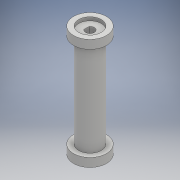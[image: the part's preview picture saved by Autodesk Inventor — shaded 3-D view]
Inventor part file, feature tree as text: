
AUTODESK INVENTOR PART (.ipt)
format: ipt  version: 2017 (Build 210142000, 142)  size: 198,144 bytes
history: native  units: mm
features: sketch x7, extrude x6, revolve x1
ambient origin geometry x8: Origin, YZ Plane, XZ Plane, XY Plane, X Axis, Y Axis, Z Axis, Center Point
bodies: Body1 (feature_tree)
feature tree (14):
  revolve  "Revolution2"  [1 undecoded]
  extrude  "Extrusion6"  Depth=20.0mm
  extrude  "Extrusion7"  Depth=4.0mm
  extrude  "Extrusion11"  Depth=2.5mm
  extrude  "Extrusion12"  Depth=4.0mm
  extrude  "Extrusion13"  Depth=20.0mm
  extrude  "Extrusion14"  Depth=15.0mm
  sketch  "Sketch1"  dims[d1=2.5mm d2=4.0mm]
  sketch  "Sketch6"  dims[d3=7.0mm d4=20.0mm]
  sketch  "Sketch7"  dims[d5=34.0mm d9=4.0mm]
  sketch  "Sketch11"  dims[d12=2.5mm d13=4.0mm]
  sketch  "Sketch12"  dims[d55=22.5mm d56=4.0mm]
  sketch  "Sketch13"  dims[d57=90.0deg d64=20.0mm]
  sketch  "Sketch14"  dims[d65=90.0deg d69=15.0mm d71=15.0mm d73=5.0mm d74=0.0mm d75=2.5mm d76=5.0mm d77=5.0mm d78=26.0mm d79=0.0mm d80=3.0mm d81=3.0mm d82=3.0mm d83=3.0mm d90=19.0mm d91=100.0mm d92=0.0mm d93=2.0mm d94=0.0mm d95=30.0mm d96=0.0mm d97=19.0mm d98=13.0mm d99=2.0mm d100=0.0mm]
note: 1 required parameter value undecoded (feature->parameter linkage not recoverable at this tier; creation-order binding heuristic only, values carry confidence <= 0.55)
